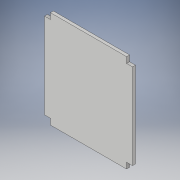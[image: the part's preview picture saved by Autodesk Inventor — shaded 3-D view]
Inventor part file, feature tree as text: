
AUTODESK INVENTOR PART (.ipt)
format: ipt  version: 2018 (Build 220112000, 112)  size: 102,912 bytes
history: native  units: in
note: dims shown in document units (in); Inventor stores cm internally (conversion verified against a paired STEP export)
features: extrude x1, sketch x1
ambient origin geometry x8: Origin, YZ Plane, XZ Plane, XY Plane, X Axis, Y Axis, Z Axis, Center Point
bodies: Solid1 (feature_tree)
feature tree (2):
  extrude  "Extrusion1"  Depth=2.0in
  sketch  "Sketch1"  dims[d0=25.81in d1=2.0in d2=2.0in d3=29.0in d4=2.0in d5=2.0in d6=2.0in d7=2.0in d8=1.0in d9=0.0in]
